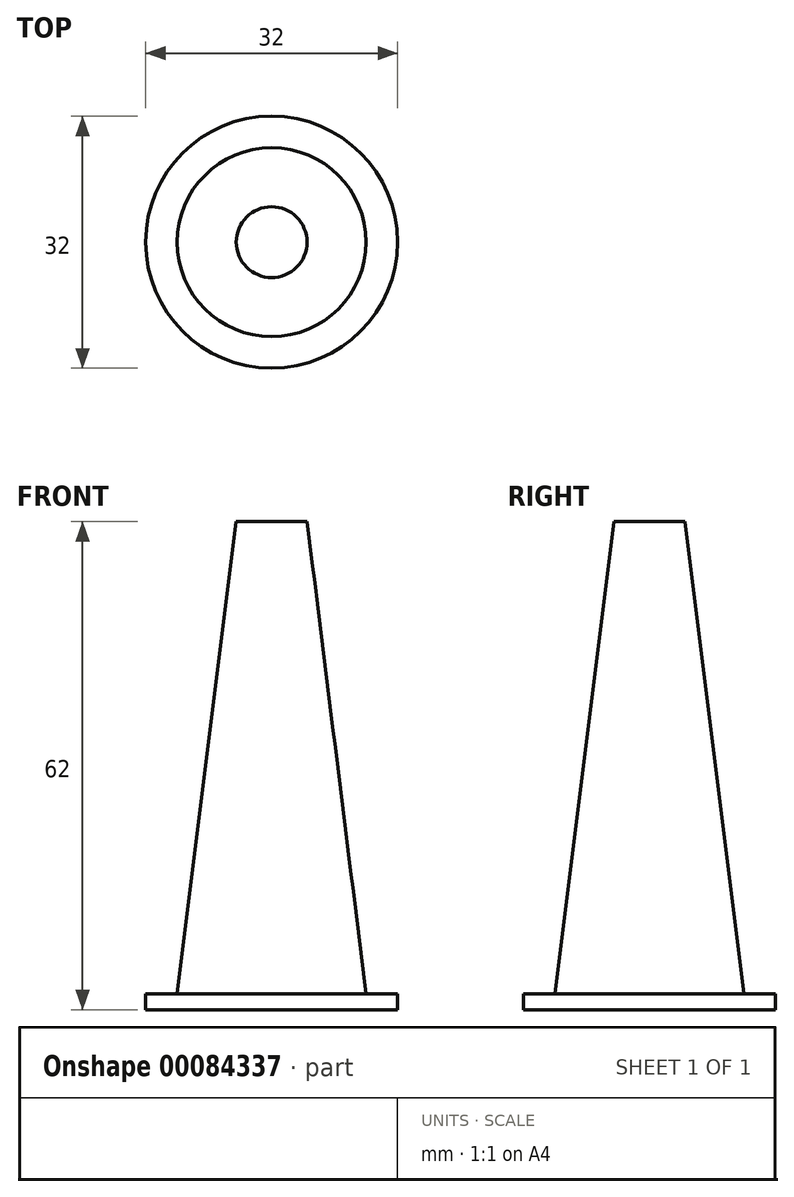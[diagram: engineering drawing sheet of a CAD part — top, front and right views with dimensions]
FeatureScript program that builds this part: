
annotation { "Feature Type Name" : "Feature", "Feature Type Description" : "" }
export const myFeature = defineFeature(function(context is Context, id is Id, definition is map)
    precondition{}
    {
        {
            var Q0;
            Q0=qCreatedBy(makeId("Top.planeOp"),FACE);
            var sketch = newSketch(context, id + "F0", { "sketchPlane" : qUnion([Q0])});
            skCircle(sketch, "E0", {"center": v(0, 0) * mm, "radius": 12 * mm});
            skSolve(sketch);
        }
        {
            var Q0;
            Q0=qCreatedBy(makeId("Top.planeOp"),FACE);
            cPlane(context, id + "F1", {"entities" : qUnion([Q0]), "cplaneType" : CPlaneType.OFFSET, "offset" : 60 * mm, "width" : 150 * mm, "height" : 150 * mm});
        }
        {
            var Q0;
            Q0=qCreatedBy(id+"F1.planeOp",FACE);
            var sketch = newSketch(context, id + "F2", { "sketchPlane" : qUnion([Q0])});
            skCircle(sketch, "E1", {"center": v(0, 0) * mm, "radius": 4.5 * mm});
            skSolve(sketch);
        }
        {
            var Q0;
            Q0=makeQuery(id+"F2.imprint","IMPRINT",FACE,{"disambiguationData":[TD([[makeQuery(id+"F2.imprint","IMPRINT",EDGE,{"derivedFrom":sQuery(id+"F2.wireOp",EDGE,"E1")}),1.0]])]});
            var Q1;
            Q1=makeQuery(id+"F0.imprint","IMPRINT",FACE,{"disambiguationData":[TD([[makeQuery(id+"F0.imprint","IMPRINT",EDGE,{"derivedFrom":sQuery(id+"F0.wireOp",EDGE,"E0")}),1.0]])]});
            loft(context, id + "F3", {"sheetProfilesArray" : [{ "sheetProfileEntities" : qUnion([Q0]) }, { "sheetProfileEntities" : qUnion([Q1]) }]});
        }
        {
            var Q0;
            Q0=qCreatedBy(makeId("Top.planeOp"),FACE);
            var sketch = newSketch(context, id + "F4", { "sketchPlane" : qUnion([Q0])});
            skCircle(sketch, "E2", {"center": v(0, 0) * mm, "radius": 16 * mm});
            skSolve(sketch);
        }
        {
            var Q0;
            Q0=makeQuery(id+"F4.imprint","IMPRINT",FACE,{"disambiguationData":[TD([[makeQuery(id+"F4.imprint","IMPRINT",EDGE,{"derivedFrom":sQuery(id+"F4.wireOp",EDGE,"E2")}),1.0]])]});
            extrude(context, id + "F5", {"entities" : qUnion([Q0]), "operationType" : NewBodyOperationType.ADD, "oppositeDirection" : true, "depth" : 2 * mm});
        }
    });
